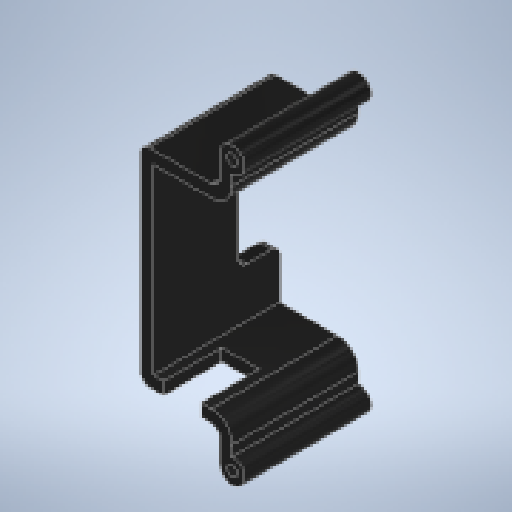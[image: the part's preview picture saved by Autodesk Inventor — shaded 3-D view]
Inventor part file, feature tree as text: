
AUTODESK INVENTOR PART (.ipt)
format: ipt  version: 2025.1 (Build 291241000, 241)  size: 210,432 bytes
history: native  units: mm
features: other x5, sketch x3, extrude x3, reference x3, fillet x1
ambient origin geometry x8: Origin, YZ Plane, XZ Plane, XY Plane, X Axis, Y Axis, Z Axis, Center Point
bodies: Body1 (feature_tree)
feature tree (15):
  other  "ソリッド1"
  sketch  "スケッチ1"
  other  "作業平面1"
  extrude  "押し出し1"  Depth=2.6mm
  extrude  "押し出し2"  Depth=2.6mm
  fillet  "フィレット1"  Radius=6.0mm
  extrude  "押し出し3"  Depth=6.0mm
  reference  "参照1"
  reference  "参照2"
  reference  "参照3"
  sketch  "スケッチ2"
  sketch  "スケッチ3"
  other  "<userpath>\Documents\Inventor\Vixen\doutai.iam"
  other  "doutai.iam"
  other  "kataue:1"
